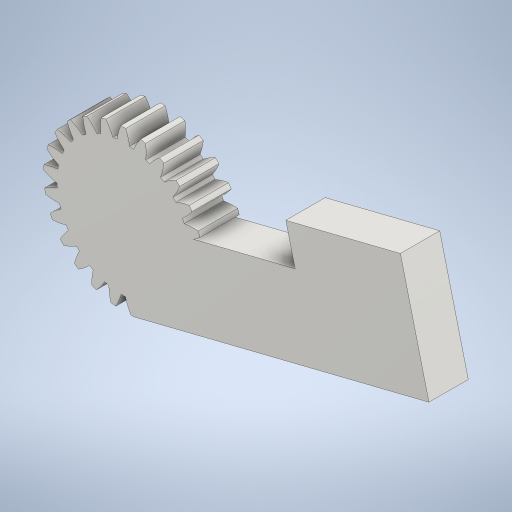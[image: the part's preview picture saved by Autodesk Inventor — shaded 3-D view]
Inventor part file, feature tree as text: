
AUTODESK INVENTOR PART (.ipt)
format: ipt  version: 2024 (Build 280153000, 153)  size: 911,872 bytes
history: native  units: mm (DEFAULTED — no unit token found)
features: plane x3, other x3, extrude x2, sketch x2, projected_geometry x1
ambient origin geometry x8: Origin, YZ Plane, XZ Plane, XY Plane, X Axis, Y Axis, Z Axis, Center Point
bodies: Solid1 (feature_tree)
feature tree (11):
  extrude  "Extrusion1"  Depth=6.666667mm TaperAngle=0.0deg
  plane  "Work Plane2"
  plane  "Work Plane8"
  plane  "Work Plane9"
  other  "Spur Gear"
  extrude  "Extrusion2"  Depth=10.0mm TaperAngle=0.0deg
  sketch  "Sketch1"  dims[d0=27.0mm d1=6.666667mm d2=0.0mm]
  other  "Srf1"
  sketch  "Sketch4"  dims[d3=25.0mm d4=10.0mm d5=0.0mm d16=25.0mm d17=0.0mm d34=1.256637mm d39=0.0mm d41=0.0mm d43=25.0mm d46=25.0mm d47=0.0mm d48=0.0mm d50=20.0mm d51=20.0mm d53=10.0mm d54=0.0mm d59=13.264502mm d60=6.307mm d61=30.0mm d62=90.0deg d63=90.0deg d64=90.0deg d65=50.0mm]
  projected_geometry  "Projected Loop1"
  other  "Pitch Diameter"
